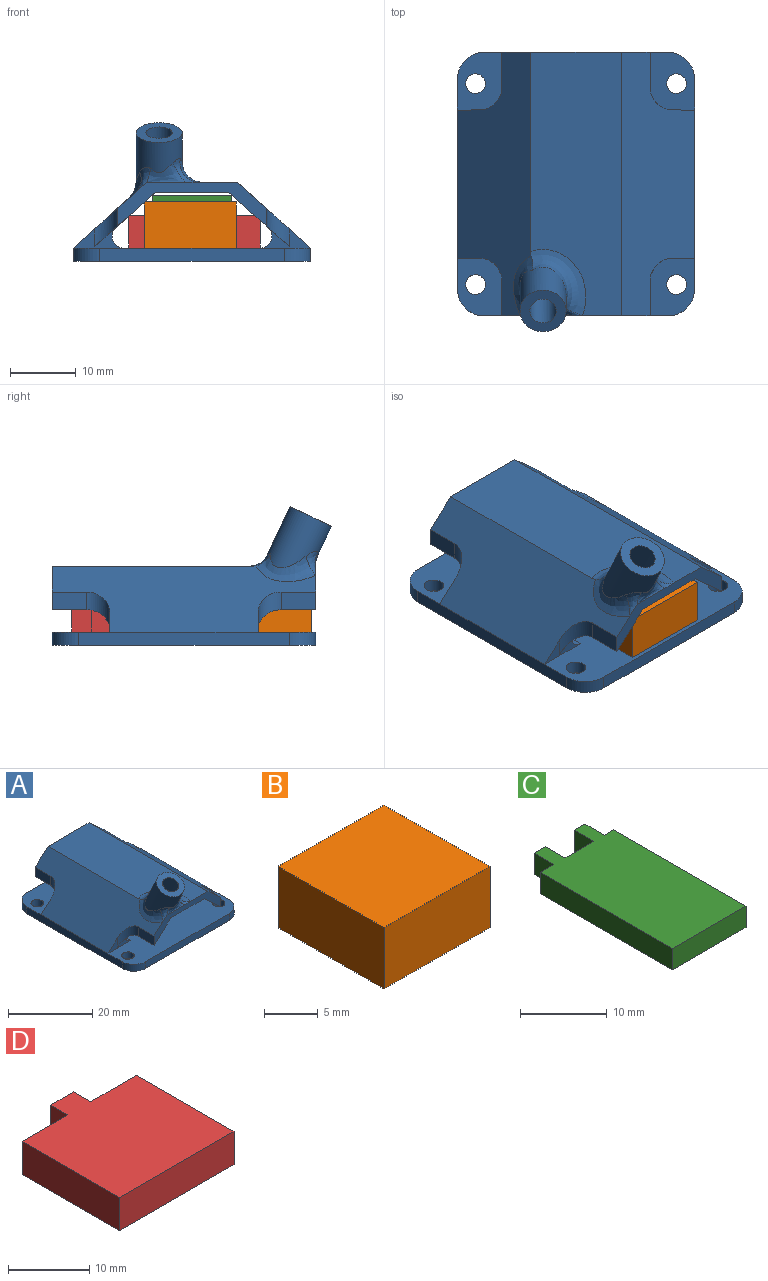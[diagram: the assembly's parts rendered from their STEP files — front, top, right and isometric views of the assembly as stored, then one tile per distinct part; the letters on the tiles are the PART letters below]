
ASSEMBLY  parts=4 mates=3
PART A: 44 faces, bbox 37.3x43.8x22.4 mm
  f0: bspline ~3.79x3.57mm, area 4.5mm2, adj f3,f35,f36,f37
  f1: cylinder r=2mm len=12.23mm, axis (0,0.43,-0.9), area 130.4mm2, adj f6,f18,f34
  f2: plane 28x2mm, normal (0,-1,0), area 56mm2, adj f10,f17,f30,f31
  f3: plane 23.22x7.33mm, normal (0,-1,0), area 45.7mm2, adj f0,f6,f7,f8,f9,f18,f19,f23
  f4: plane 28x2mm, normal (0,1,0), area 56mm2, adj f10,f17,f32,f33
  f5: plane 22.5x6.61mm, normal (0,1,0), area 45.7mm2, adj f6,f7,f8,f9,f18,f19,f21,f27
  f6: plane 41.33x10.5mm, normal (0.67,0,-0.74), area 315.1mm2, adj f1,f3,f5,f18,f20,f21,f22,f23
  f7: plane 41.33x10.5mm, normal (-0.67,0,-0.74), area 321.1mm2, adj f3,f5,f18,f24,f25,f26,f27,f28
  f8: plane 41.33x12.43mm, normal (0.67,0,0.74), area 445.9mm2, adj f3,f5,f12,f19,f24,f25,f26,f27
  f9: plane 41.33x12.53mm, normal (-0.67,0,0.74), area 420.7mm2, adj f3,f5,f11,f19,f20,f21,f22,f23
  f10: plane 40x36mm, normal (0,0,1), area 1052.5mm2, adj f2,f4,f11,f12,f13,f14,f15,f16
  f11: plane 32x2mm, normal (-1,0,0), area 64mm2, adj f9,f10,f17,f30,f33
  f12: plane 32x2mm, normal (1,0,0), area 64mm2, adj f8,f10,f17,f31,f32
  f13: cylinder r=1.5mm len=3mm, axis (0,0,-1), area 18.8mm2, adj f10,f17
  f14: cylinder r=1.5mm len=3mm, axis (0,0,-1), area 18.8mm2, adj f10,f17
  f15: cylinder r=1.5mm len=3mm, axis (0,0,-1), area 18.8mm2, adj f10,f17
  f16: cylinder r=1.5mm len=3mm, axis (0,0,-1), area 18.8mm2, adj f10,f17
  f17: plane 40x36mm, normal (0,0,-1), area 1398mm2, adj f2,f4,f11,f12,f13,f14,f15,f16
  f18: plane 40.02x11.16mm, normal (0,0,-1), area 436.2mm2, adj f1,f3,f5,f6,f7
  f19: plane 40x13.79mm, normal (0,0,1), area 477.8mm2, adj f3,f5,f8,f9,f37
  f20: plane 7.68x3.14mm, normal (0,1,0), area 9.3mm2, adj f6,f9,f10,f29,f43
  f21: plane 5.25x2.69mm, normal (-1,0,0), area 14.1mm2, adj f5,f6,f9,f43
  f22: plane 7.68x3.14mm, normal (0,-1,0), area 9.3mm2, adj f6,f9,f10,f29,f42
  f23: plane 5.25x2.69mm, normal (-1,0,0), area 14.1mm2, adj f3,f6,f9,f42
  f24: plane 7.68x3.14mm, normal (0,-1,0), area 9.3mm2, adj f7,f8,f10,f28,f40
  f25: plane 5.25x2.69mm, normal (1,0,0), area 14.1mm2, adj f3,f7,f8,f40
  f26: plane 7.68x3.14mm, normal (0,1,0), area 9.3mm2, adj f7,f8,f10,f28,f41
  f27: plane 5.25x2.69mm, normal (1,0,0), area 14.1mm2, adj f5,f7,f8,f41
  f28: cylinder r=1.8mm len=22.5mm, axis (0,-1,0), area 97.5mm2, adj f7,f10,f24,f26
  f29: cylinder r=1.8mm len=22.5mm, axis (0,-1,0), area 97.5mm2, adj f6,f10,f20,f22
  f30: cylinder r=4mm len=4mm, axis (0,0,1), area 12.6mm2, adj f2,f10,f11,f17
  f31: cylinder r=4mm len=4mm, axis (0,0,-1), area 12.6mm2, adj f2,f10,f12,f17
  f32: cylinder r=4mm len=4mm, axis (0,0,1), area 12.6mm2, adj f4,f10,f12,f17
  f33: cylinder r=4mm len=4mm, axis (0,0,-1), area 12.6mm2, adj f4,f10,f11,f17
  f34: plane 7x6.33mm, normal (0,-0.43,0.9), area 25.9mm2, adj f1,f35
  f35: cylinder r=3.5mm len=11.28mm, axis (0,0.43,-0.9), area 135.4mm2, adj f0,f34,f36,f37,f38,f39
  f36: bspline ~8.01x3.26mm, area 9.9mm2, adj f0,f3,f35,f38
  f37: bspline ~10.06x9.55mm, area 48.8mm2, adj f0,f9,f19,f35,f39
  f38: bspline ~3.62x2.26mm, area 4.9mm2, adj f3,f35,f36,f39
  f39: bspline ~9.22x4.2mm, area 24.2mm2, adj f9,f35,f37,f38
  f40: cylinder r=3.5mm len=5.84mm, axis (0,0,1), area 14.8mm2, adj f7,f8,f24,f25
  f41: cylinder r=3.5mm len=5.84mm, axis (0,0,1), area 14.8mm2, adj f7,f8,f26,f27
  f42: cylinder r=3.5mm len=5.84mm, axis (0,0,1), area 14.8mm2, adj f6,f9,f22,f23
  f43: cylinder r=3.5mm len=5.84mm, axis (0,0,1), area 14.8mm2, adj f6,f9,f20,f21
PART B: 6 faces, bbox 14x14x7 mm
  f0: plane 14x7mm, normal (-1,0,0), area 98mm2, adj f1,f3,f4,f5
  f1: plane 14x7mm, normal (0,-1,0), area 98mm2, adj f0,f2,f4,f5
  f2: plane 14x7mm, normal (1,0,0), area 98mm2, adj f1,f3,f4,f5
  f3: plane 14x7mm, normal (0,1,0), area 98mm2, adj f0,f2,f4,f5
  f4: plane 14x14mm, normal (0,0,1), area 196mm2, adj f0,f1,f2,f3
  f5: plane 14x14mm, normal (0,0,-1), area 196mm2, adj f0,f1,f2,f3
PART C: 14 faces, bbox 12x24.7x3 mm
  f0: plane 3.16x3mm, normal (-1,0,0), area 9.5mm2, adj f1,f11,f12,f13
  f1: plane 4.7x3mm, normal (0,1,0), area 14.1mm2, adj f0,f2,f12,f13
  f2: plane 3.22x3mm, normal (1,0,0), area 9.6mm2, adj f1,f3,f12,f13
  f3: plane 3x1.82mm, normal (0,1,0), area 5.5mm2, adj f2,f4,f12,f13
  f4: plane 3.22x3mm, normal (-1,0,0), area 9.6mm2, adj f3,f5,f12,f13
  f5: plane 3x2.23mm, normal (0,1,0), area 6.7mm2, adj f4,f6,f12,f13
  f6: plane 21.5x3mm, normal (-1,0,0), area 64.5mm2, adj f5,f7,f12,f13
  f7: plane 12x3mm, normal (0,-1,0), area 36mm2, adj f6,f8,f12,f13
  f8: plane 21.5x3mm, normal (1,0,0), area 64.5mm2, adj f7,f9,f12,f13
  f9: plane 3x1.54mm, normal (0,1,0), area 4.6mm2, adj f8,f10,f12,f13
  f10: plane 3.16x3mm, normal (1,0,0), area 9.5mm2, adj f9,f11,f12,f13
  f11: plane 3x1.71mm, normal (0,1,0), area 5.1mm2, adj f0,f10,f12,f13
  f12: plane 24.72x12mm, normal (0,0,1), area 269.3mm2, adj f0,f1,f2,f3,f4,f5,f6,f7
  f13: plane 24.72x12mm, normal (0,0,-1), area 269.3mm2, adj f0,f1,f2,f3,f4,f5,f6,f7
PART D: 10 faces, bbox 20x20x5 mm
  f0: plane 8x5mm, normal (0,1,0), area 40mm2, adj f1,f7,f8,f9
  f1: plane 17x5mm, normal (-1,0,0), area 85mm2, adj f0,f2,f8,f9
  f2: plane 20x5mm, normal (0,-1,0), area 100mm2, adj f1,f3,f8,f9
  f3: plane 17x5mm, normal (1,0,0), area 85mm2, adj f2,f4,f8,f9
  f4: plane 8x5mm, normal (0,1,0), area 40mm2, adj f3,f5,f8,f9
  f5: plane 5x3mm, normal (1,0,0), area 15mm2, adj f4,f6,f8,f9
  f6: plane 5x4mm, normal (0,1,0), area 20mm2, adj f5,f7,f8,f9
  f7: plane 5x3mm, normal (-1,0,0), area 15mm2, adj f0,f6,f8,f9
  f8: plane 20x20mm, normal (0,0,1), area 352mm2, adj f0,f1,f2,f3,f4,f5,f6,f7
  f9: plane 20x20mm, normal (0,0,-1), area 352mm2, adj f0,f1,f2,f3,f4,f5,f6,f7
PLACE A t=(-2.14,15.84,-14.14)mm
PLACE B t=(3.1,13.56,-14.14)mm
PLACE C t=(-13.94,20.87,-9.14)mm
PLACE D t=(6.39,14.02,-14.14)mm
MATE planar D.f8 <-> C.f13  axis (0,0,1) through (-1.75,12.86,-7.14)mm
MATE planar A.f10 <-> D.f9  axis (0,0,1) through (-2.14,15.84,-12.14)mm
MATE planar A.f10 <-> B.f5  axis (0,0,1) through (-2.14,15.84,-12.14)mm
